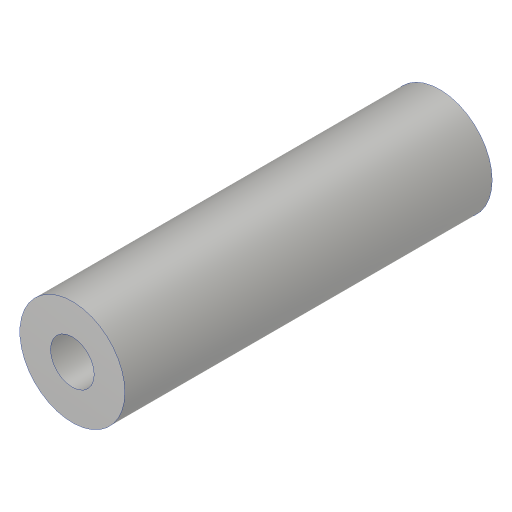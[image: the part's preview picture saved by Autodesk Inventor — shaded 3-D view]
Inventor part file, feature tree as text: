
AUTODESK INVENTOR PART (.ipt)
format: ipt  version: 2023.4 (Build 274418000, 418)  size: 122,368 bytes
history: native  units: in
note: dims shown in document units (in); Inventor stores cm internally (conversion verified against a paired STEP export)
features: extrude x1, hole x1
ambient origin geometry x8: Origin, YZ Plane, XZ Plane, XY Plane, X Axis, Y Axis, Z Axis, Center Point
bodies: Solid1 (feature_tree)
feature tree (2):
  extrude  "Extrusion1"  Depth=1.311in
  hole  "Hole1"  [1 undecoded]
note: 1 required parameter value undecoded (feature->parameter linkage not recoverable at this tier; creation-order binding heuristic only, values carry confidence <= 0.55)
